# Revit family: LIANO II PULL DOWN SENSOR SINK MIXER
name_source: partatom
category: Specialty Equipment
units: mm (PartAtom-declared; Revit-internal decimal feet)

## family parameters
Cut with Voids When Loaded = No
Host = Face
OmniClass Number = 23.45.55.14
OmniClass Title = Single Faucets
Part Type = Normal
Room Calculation Point = No
Round Connector Dimension = Use Radius
Shared = No

## types (2) — shared parameters
Assembly Code = C1030220
Default Elevation = 1000 mm  [stored 3.28084 ft]
Description = LIANO II PULL DOWN SENSOR SINK MIXER CHROME
Manufacturer = GWA Bathrooms & Kitchens
Material_Base = GWA_Metal-Chrome
Material_Hose = GWA-Plastic-Black
Material_Sensor = GWA-Acrylic-Black
Model = 96385C56A
URL = https://www.caroma.com.au

## per-type parameters (varying)
| type | Blade_Handle | Pin_Handle |
| LIANO II PULL DOWN SENSOR SINK MIXER CHROME PIN | No | Yes |
| LIANO II PULL DOWN SENSOR SINK MIXER CHROME BLADE | Yes | No |

note: [stored X ft] marks values corroborated as IEEE doubles in the binary element streams (Revit-internal decimal feet)

## geometry (parser evidence)
native form markers: Sweep x2
no freeform markers — native parametric forms only
